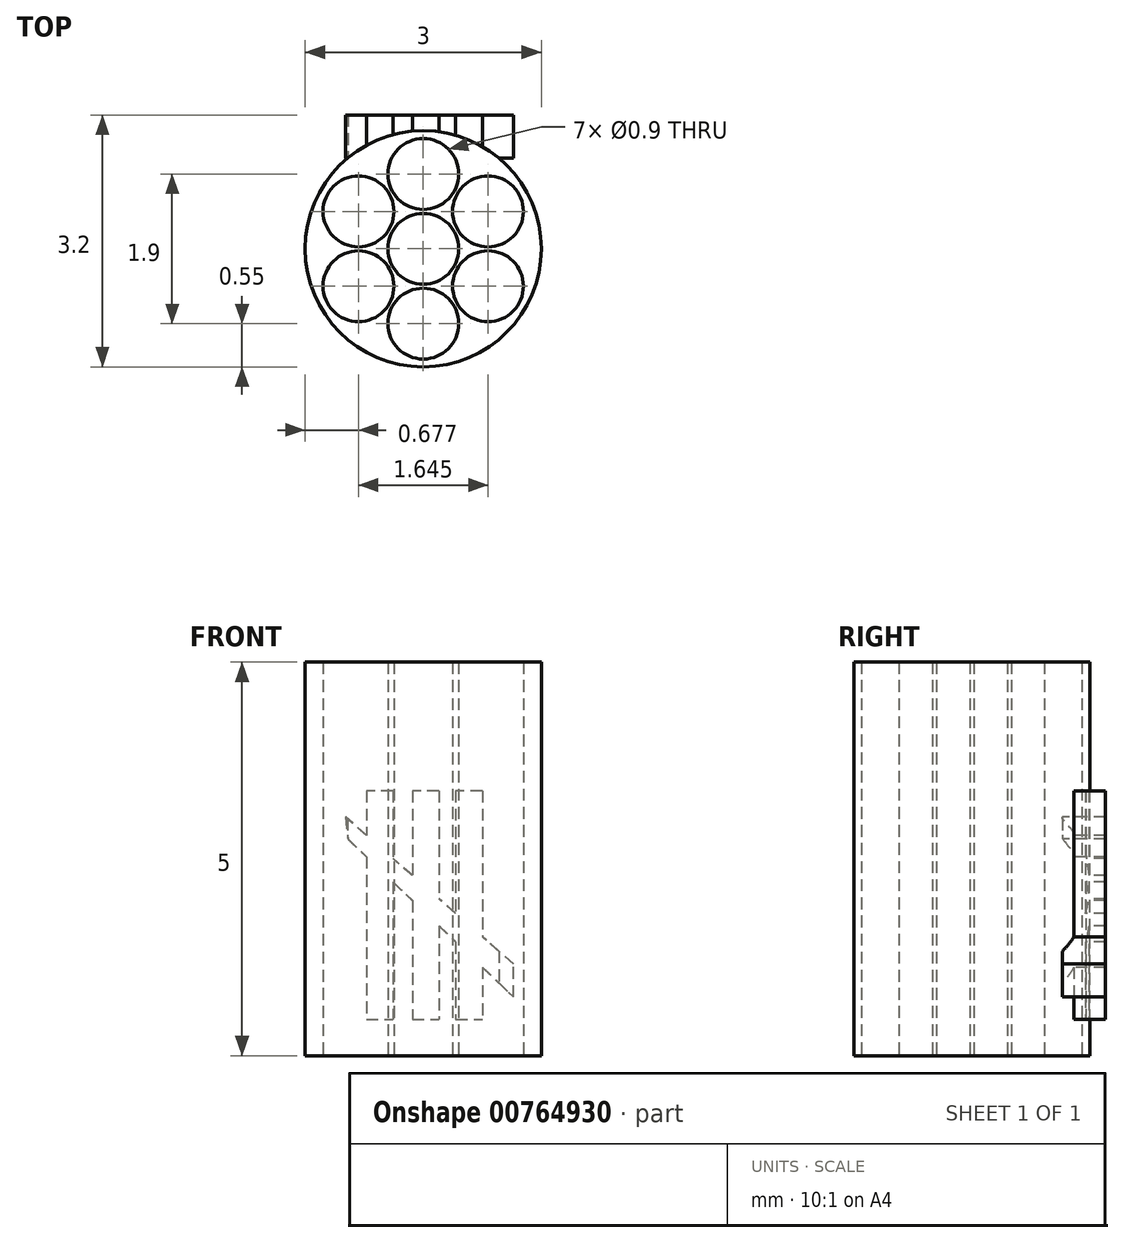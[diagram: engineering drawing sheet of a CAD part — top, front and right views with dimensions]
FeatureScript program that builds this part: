
annotation { "Feature Type Name" : "Feature", "Feature Type Description" : "" }
export const myFeature = defineFeature(function(context is Context, id is Id, definition is map)
    precondition{}
    {
        {
            var Q0;
            Q0=qCreatedBy(makeId("Top.planeOp"),FACE);
            var sketch = newSketch(context, id + "F0", { "sketchPlane" : qUnion([Q0])});
            skCircle(sketch, "E0", {"center": v(0, 0) * mm, "radius": 0.95 * mm});
            skCircle(sketch, "E1.cCircle", {"center": v(0, 0) * mm, "radius": 0.95 * mm, "construction": true});
            skLineSegment(sketch, "E1.0", {"start": v(0, 0.95) * mm, "end": v(0.82, 0.48) * mm});
            skLineSegment(sketch, "E1.1", {"start": v(0.82, 0.48) * mm, "end": v(0.82, -0.48) * mm});
            skLineSegment(sketch, "E1.2", {"start": v(0.82, -0.48) * mm, "end": v(0, -0.95) * mm});
            skLineSegment(sketch, "E1.3", {"start": v(0, -0.95) * mm, "end": v(-0.82, -0.48) * mm});
            skLineSegment(sketch, "E1.4", {"start": v(-0.82, -0.48) * mm, "end": v(-0.82, 0.47) * mm});
            skLineSegment(sketch, "E1.5", {"start": v(-0.82, 0.47) * mm, "end": v(0, 0.95) * mm});
            skSolve(sketch);
        }
        {
            var Q0;
            Q0=qCreatedBy(makeId("Top.planeOp"),FACE);
            var sketch = newSketch(context, id + "F1", { "sketchPlane" : qUnion([Q0])});
            skCircle(sketch, "E2", {"center": v(0, 0) * mm, "radius": 0.45 * mm});
            skCircle(sketch, "E3", {"center": v(0, 0.95) * mm, "radius": 0.45 * mm});
            skCircle(sketch, "E4", {"center": v(0.82, 0.48) * mm, "radius": 0.45 * mm});
            skCircle(sketch, "E5", {"center": v(0.82, -0.48) * mm, "radius": 0.45 * mm});
            skCircle(sketch, "E6", {"center": v(0, -0.95) * mm, "radius": 0.45 * mm});
            skCircle(sketch, "E7", {"center": v(-0.82, -0.48) * mm, "radius": 0.45 * mm});
            skCircle(sketch, "E8", {"center": v(-0.82, 0.47) * mm, "radius": 0.45 * mm});
            skSolve(sketch);
        }
        {
            var Q0;
            Q0=qCreatedBy(makeId("Top.planeOp"),FACE);
            var sketch = newSketch(context, id + "F2", { "sketchPlane" : qUnion([Q0])});
            skCircle(sketch, "E9", {"center": v(0, 0) * mm, "radius": 1.5 * mm});
            skSolve(sketch);
        }
        {
            var Q0;
            Q0=qSketchRegion(id+"F2",true);
            extrude(context, id + "F3", {"entities" : qUnion([Q0]), "depth" : 5 * mm, "offsetDistance" : 25 * mm});
        }
        {
            var Q0;
            Q0=makeQuery(id+"F3.opExtrude","CAP_FACE",FACE,{"disambiguationData":[OSD([sQuery(id+"F2.wireOp",EDGE,"E9")])],"isStart":false});
            var sketch = newSketch(context, id + "F4", { "sketchPlane" : qUnion([Q0])});
            skPoint(sketch, "E10", {"position": v(0, -1.5) * mm});
            skPoint(sketch, "E11", {"position": v(-0.36, -1.5) * mm});
            skPoint(sketch, "E12", {"position": v(0.42, -1.5) * mm});
            skSolve(sketch);
        }
        {
            var Q0;
            Q0=makeQuery(id+"F3.opExtrude","CAP_FACE",FACE,{"disambiguationData":[OSD([sQuery(id+"F2.wireOp",EDGE,"E9")])],"isStart":true});
            var sketch = newSketch(context, id + "F5", { "sketchPlane" : qUnion([Q0])});
            skPoint(sketch, "E13", {"position": v(0, 1.5) * mm});
            skPoint(sketch, "E14", {"position": v(-0.36, 1.5) * mm});
            skPoint(sketch, "E15", {"position": v(0.42, 1.5) * mm});
            skSolve(sketch);
        }
        {
            var Q0;
            Q0=sQuery(id+"F4.wireOp",VERTEX,"E10");
            var Q1;
            Q1=sQuery(id+"F5.wireOp",VERTEX,"E13");
            var Q2;
            Q2=sQuery(id+"F5.wireOp",VERTEX,"E15");
            cPlane(context, id + "F6", {"entities" : qUnion([Q0, Q1, Q2]), "cplaneType" : CPlaneType.THREE_POINT, "offset" : 0 * mm, "oppositeDirection" : true, "width" : 150 * mm, "height" : 150 * mm});
        }
        {
            var Q0;
            Q0=qCreatedBy(id+"F6.planeOp",FACE);
            cPlane(context, id + "F7", {"entities" : qUnion([Q0]), "cplaneType" : CPlaneType.OFFSET, "offset" : 2.65 * mm, "width" : 150 * mm, "height" : 150 * mm});
        }
        {
            var Q0;
            Q0=qCreatedBy(id+"F7.planeOp",FACE);
            var sketch = newSketch(context, id + "F8", { "sketchPlane" : qUnion([Q0])});
            skText(sketch, "E16", { "text": "II", "fontName": "OpenSans-Regular.ttf"});
            skText(sketch, "E17", { "text": "I", "fontName": "OpenSans-Regular.ttf"});
            skLineSegment(sketch, "E18", {"start": v(0.99, 3.03) * mm, "end": v(0.96, 2.75) * mm});
            skLineSegment(sketch, "E19", {"start": v(0.96, 2.75) * mm, "end": v(-1.15, 0.74) * mm});
            skLineSegment(sketch, "E20", {"start": v(-1.15, 0.74) * mm, "end": v(-1.15, 1.16) * mm});
            skLineSegment(sketch, "E21", {"start": v(-1.15, 1.16) * mm, "end": v(0.99, 3.03) * mm});
            const initialGuessF8  = {"E16": [-0.00115, 0.00046, 1, 0, 0.00293], "E17": [-0.0006, 0.00046, 1, 0, 0.00293]};
            skSetInitialGuess(sketch, initialGuessF8);
            skSolve(sketch);
        }
        {
            var Q0;
            Q0=qSketchRegion(id+"F8",true);
            extrude(context, id + "F9", {"entities" : qUnion([Q0]), "operationType" : NewBodyOperationType.ADD, "depth" : 0.55 * mm, "offsetDistance" : 25 * mm});
        }
        {
            var Q0;
            Q0=qSketchRegion(id+"F1",true);
            extrude(context, id + "F10", {"entities" : qUnion([Q0]), "operationType" : NewBodyOperationType.REMOVE, "endBound" : BoundingType.THROUGH_ALL, "depth" : 25 * mm, "offsetDistance" : 25 * mm});
        }
    });
